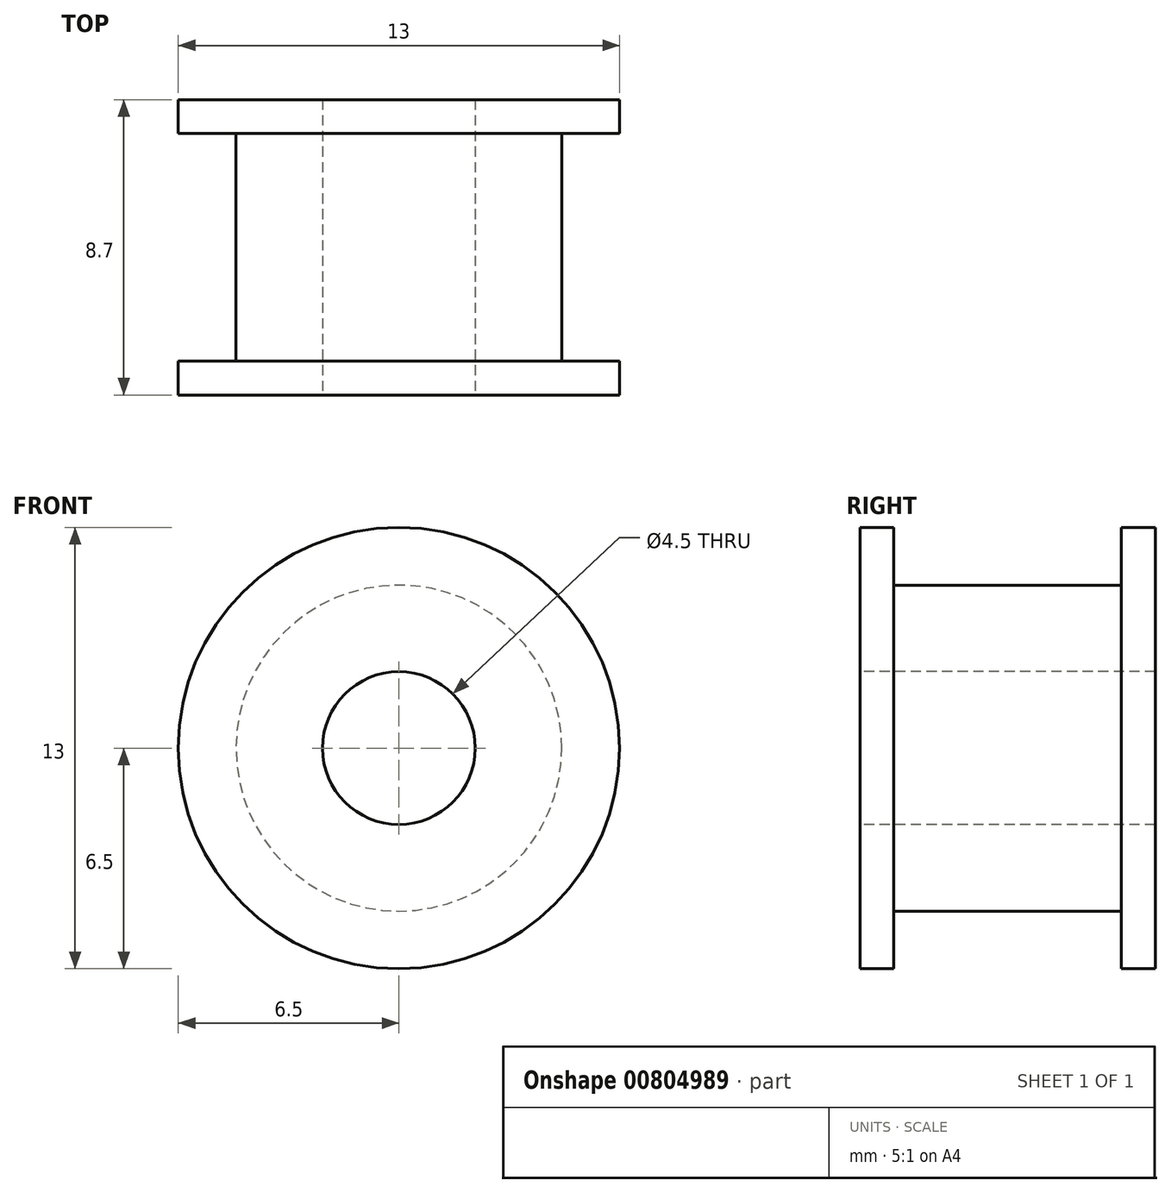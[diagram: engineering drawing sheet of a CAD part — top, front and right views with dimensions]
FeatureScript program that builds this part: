
annotation { "Feature Type Name" : "Feature", "Feature Type Description" : "" }
export const myFeature = defineFeature(function(context is Context, id is Id, definition is map)
    precondition{}
    {
        {
            var Q0;
            Q0=qCreatedBy(makeId("Right.planeOp"),FACE);
            var sketch = newSketch(context, id + "F0", { "sketchPlane" : qUnion([Q0])});
            skLineSegment(sketch, "E0", {"start": v(-4.35, 6.5) * mm, "end": v(-4.35, 2.25) * mm});
            skLineSegment(sketch, "E1", {"start": v(-4.35, 2.25) * mm, "end": v(4.35, 2.25) * mm});
            skLineSegment(sketch, "E2", {"start": v(4.35, 6.5) * mm, "end": v(4.35, 2.25) * mm});
            skLineSegment(sketch, "E3", {"start": v(-4.25, 0) * mm, "end": v(4.18, 0) * mm, "construction": true});
            skLineSegment(sketch, "E4", {"start": v(-4.35, 6.5) * mm, "end": v(-3.35, 6.5) * mm});
            skLineSegment(sketch, "E5", {"start": v(-3.35, 6.5) * mm, "end": v(-3.35, 4.8) * mm});
            skLineSegment(sketch, "E6", {"start": v(-3.35, 4.8) * mm, "end": v(3.35, 4.8) * mm});
            skLineSegment(sketch, "E7", {"start": v(3.35, 4.8) * mm, "end": v(3.35, 6.5) * mm});
            skLineSegment(sketch, "E8", {"start": v(3.35, 6.5) * mm, "end": v(4.35, 6.5) * mm});
            skSolve(sketch);
        }
        {
            var Q0;
            Q0=makeQuery(id+"F0.imprint","IMPRINT",FACE,{"disambiguationData":[TD([[makeQuery(id+"F0.imprint","IMPRINT",EDGE,{"derivedFrom":sQuery(id+"F0.wireOp",EDGE,"E0")}),1.0]])]});
            var Q1;
            Q1=sQuery(id+"F0.wireOp",EDGE,"E3");
            revolve(context, id + "F1", {"entities" : qUnion([Q0]), "axis" : qUnion([Q1]), "revolveType" : RevolveType.FULL});
        }
    });
